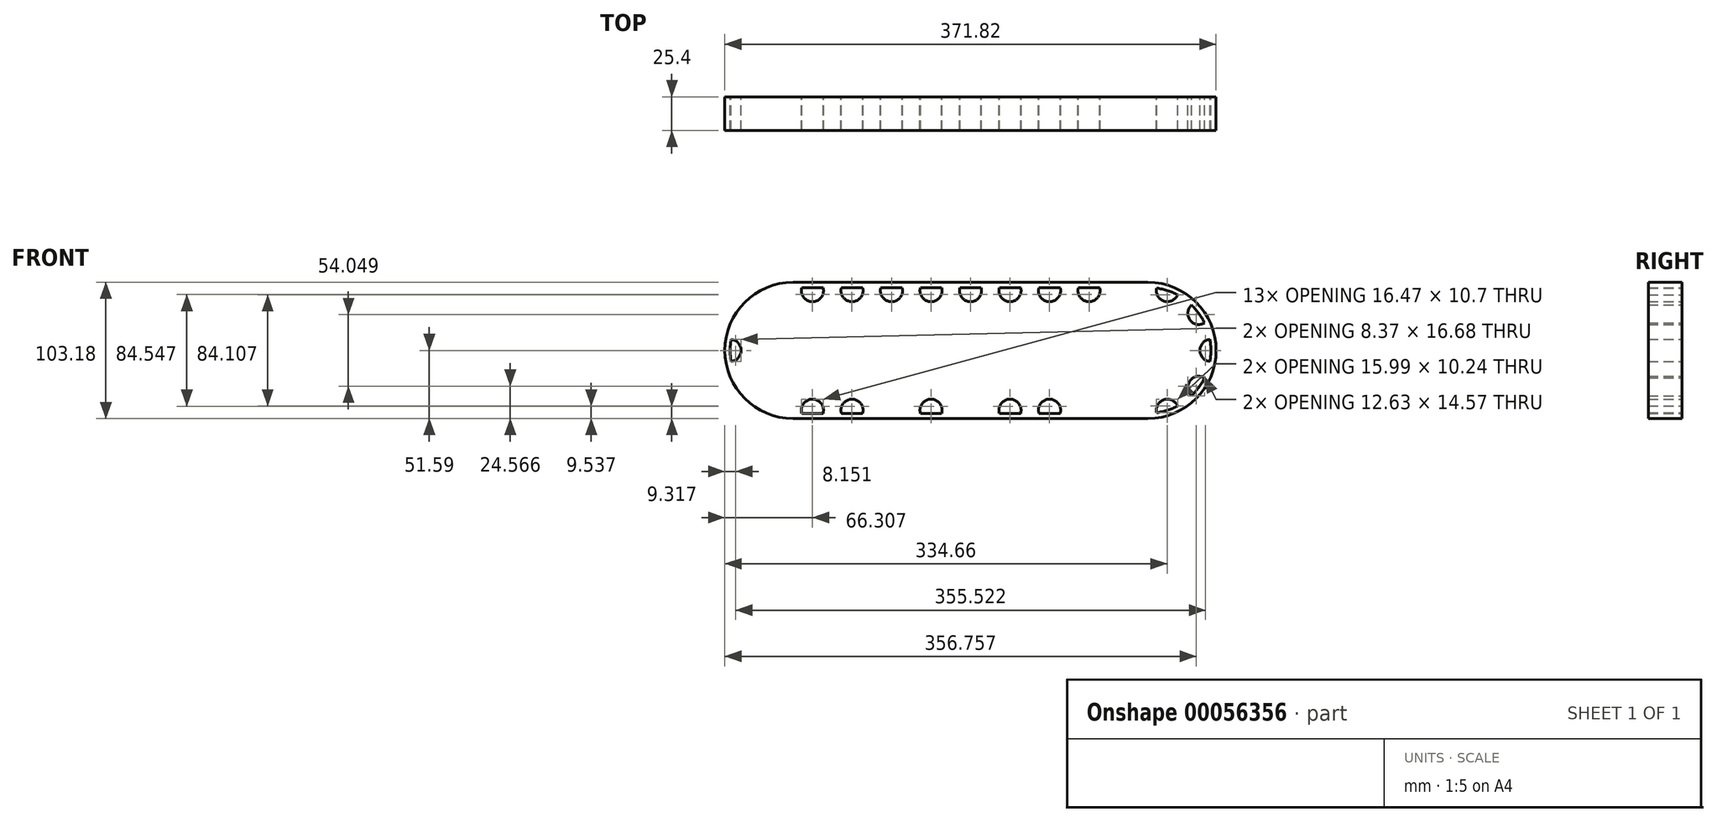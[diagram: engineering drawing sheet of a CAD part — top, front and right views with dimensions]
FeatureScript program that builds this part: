
annotation { "Feature Type Name" : "Feature", "Feature Type Description" : "" }
export const myFeature = defineFeature(function(context is Context, id is Id, definition is map)
    precondition{}
    {
        {
            var Q0;
            Q0=qCreatedBy(makeId("Front.planeOp"),FACE);
            var sketch = newSketch(context, id + "F0", { "sketchPlane" : qUnion([Q0])});
            skCircle(sketch, "E0", {"center": v(0, 0) * mm, "radius": 9.53 * mm});
            skCircle(sketch, "E1", {"center": v(0, 0) * mm, "radius": 15.88 * mm});
            skCircle(sketch, "E2", {"center": v(0, 0) * mm, "radius": 25.4 * mm});
            skCircle(sketch, "E3", {"center": v(0, 0) * mm, "radius": 38.1 * mm});
            skArc(sketch, "E4", {"start": v(5.87, 47.26) * mm, "mid": v(0, 47.63) * mm, "end": v(-5.87, 47.26) * mm});
            skLineSegment(sketch, "E5", {"start": v(-5.87, 47.26) * mm, "end": v(-7.62, 37.33) * mm});
            skLineSegment(sketch, "E6", {"start": v(5.87, 47.26) * mm, "end": v(7.62, 37.33) * mm});
            skLineSegment(sketch, "E7", {"start": v(-3.98, 25.09) * mm, "end": v(-3.98, 15.37) * mm, "construction": true});
            skLineSegment(sketch, "E8", {"start": v(3.98, 25.09) * mm, "end": v(3.98, 15.37) * mm, "construction": true});
            skArc(sketch, "E9.1.0", {"start": v(-23.03, 41.69) * mm, "mid": v(-28, 38.53) * mm, "end": v(-32.53, 34.79) * mm});
            skLineSegment(sketch, "E9.1.1", {"start": v(-32.53, 34.79) * mm, "end": v(-28.1, 25.72) * mm});
            skLineSegment(sketch, "E9.1.2", {"start": v(-23.03, 41.69) * mm, "end": v(-15.78, 34.68) * mm});
            skArc(sketch, "E9.2.0", {"start": v(-43.14, 20.19) * mm, "mid": v(-45.3, 14.72) * mm, "end": v(-46.76, 9.02) * mm});
            skLineSegment(sketch, "E9.2.1", {"start": v(-46.76, 9.02) * mm, "end": v(-37.86, 4.29) * mm});
            skLineSegment(sketch, "E9.2.2", {"start": v(-43.14, 20.19) * mm, "end": v(-33.15, 18.78) * mm});
            skArc(sketch, "E9.3.0", {"start": v(-46.76, -9.02) * mm, "mid": v(-45.3, -14.72) * mm, "end": v(-43.14, -20.19) * mm});
            skLineSegment(sketch, "E9.3.1", {"start": v(-43.14, -20.19) * mm, "end": v(-33.15, -18.78) * mm});
            skLineSegment(sketch, "E9.3.2", {"start": v(-46.76, -9.02) * mm, "end": v(-37.86, -4.29) * mm});
            skArc(sketch, "E9.4.0", {"start": v(-32.53, -34.79) * mm, "mid": v(-28, -38.53) * mm, "end": v(-23.03, -41.69) * mm});
            skLineSegment(sketch, "E9.4.1", {"start": v(-23.03, -41.69) * mm, "end": v(-15.78, -34.68) * mm});
            skLineSegment(sketch, "E9.4.2", {"start": v(-32.53, -34.79) * mm, "end": v(-28.1, -25.72) * mm});
            skArc(sketch, "E9.5.0", {"start": v(-5.87, -47.26) * mm, "mid": v(0, -47.63) * mm, "end": v(5.87, -47.26) * mm});
            skLineSegment(sketch, "E9.5.1", {"start": v(5.87, -47.26) * mm, "end": v(7.62, -37.33) * mm});
            skLineSegment(sketch, "E9.5.2", {"start": v(-5.87, -47.26) * mm, "end": v(-7.62, -37.33) * mm});
            skArc(sketch, "E9.6.0", {"start": v(23.03, -41.69) * mm, "mid": v(28, -38.53) * mm, "end": v(32.53, -34.79) * mm});
            skLineSegment(sketch, "E9.6.1", {"start": v(32.53, -34.79) * mm, "end": v(28.1, -25.72) * mm});
            skLineSegment(sketch, "E9.6.2", {"start": v(23.03, -41.69) * mm, "end": v(15.78, -34.68) * mm});
            skArc(sketch, "E9.7.0", {"start": v(43.14, -20.19) * mm, "mid": v(45.3, -14.72) * mm, "end": v(46.76, -9.02) * mm});
            skLineSegment(sketch, "E9.7.1", {"start": v(46.76, -9.02) * mm, "end": v(37.86, -4.29) * mm});
            skLineSegment(sketch, "E9.7.2", {"start": v(43.14, -20.19) * mm, "end": v(33.15, -18.78) * mm});
            skArc(sketch, "E9.8.0", {"start": v(46.76, 9.02) * mm, "mid": v(45.3, 14.72) * mm, "end": v(43.14, 20.19) * mm});
            skLineSegment(sketch, "E9.8.1", {"start": v(43.14, 20.19) * mm, "end": v(33.15, 18.78) * mm});
            skLineSegment(sketch, "E9.8.2", {"start": v(46.76, 9.02) * mm, "end": v(37.86, 4.29) * mm});
            skArc(sketch, "E9.9.0", {"start": v(32.53, 34.79) * mm, "mid": v(28, 38.53) * mm, "end": v(23.03, 41.69) * mm});
            skLineSegment(sketch, "E9.9.1", {"start": v(23.03, 41.69) * mm, "end": v(15.78, 34.68) * mm});
            skLineSegment(sketch, "E9.9.2", {"start": v(32.53, 34.79) * mm, "end": v(28.1, 25.72) * mm});
            skLineSegment(sketch, "E10.1.0", {"start": v(-19.74, -15.99) * mm, "end": v(-11.32, -11.13) * mm, "construction": true});
            skLineSegment(sketch, "E10.1.1", {"start": v(-23.71, -9.1) * mm, "end": v(-15.3, -4.24) * mm, "construction": true});
            skLineSegment(sketch, "E10.2.0", {"start": v(23.71, -9.1) * mm, "end": v(15.3, -4.24) * mm, "construction": true});
            skLineSegment(sketch, "E10.2.1", {"start": v(19.74, -15.99) * mm, "end": v(11.32, -11.13) * mm, "construction": true});
            skSolve(sketch);
        }
        {
            var Q0;
            Q0=qCreatedBy(makeId("Front.planeOp"),FACE);
            var sketch = newSketch(context, id + "F1", { "sketchPlane" : qUnion([Q0])});
            skArc(sketch, "E11", {"start": v(23.03, 41.69) * mm, "mid": v(-10.34, 46.49) * mm, "end": v(-38.53, 28) * mm});
            skLineSegment(sketch, "E12.0", {"start": v(23.03, 41.69) * mm, "end": v(15.78, 34.68) * mm, "construction": true});
            skLineSegment(sketch, "E12.1", {"start": v(5.87, 47.26) * mm, "end": v(7.62, 37.33) * mm, "construction": true});
            skLineSegment(sketch, "E12.2", {"start": v(-5.87, 47.26) * mm, "end": v(-7.62, 37.33) * mm, "construction": true});
            skLineSegment(sketch, "E12.3", {"start": v(-23.03, 41.69) * mm, "end": v(-15.78, 34.68) * mm, "construction": true});
            skLineSegment(sketch, "E12.4", {"start": v(-32.53, 34.79) * mm, "end": v(-28.1, 25.72) * mm, "construction": true});
            skLineSegment(sketch, "E12.5", {"start": v(-43.14, 20.19) * mm, "end": v(-33.15, 18.78) * mm, "construction": true});
            skLineSegment(sketch, "E12.6", {"start": v(-46.76, 9.02) * mm, "end": v(-37.86, 4.29) * mm, "construction": true});
            skLineSegment(sketch, "E12.7", {"start": v(-46.76, -9.02) * mm, "end": v(-37.86, -4.29) * mm, "construction": true});
            skCircle(sketch, "E13", {"center": v(-14.72, 45.3) * mm, "radius": 8.37 * mm});
            skCircle(sketch, "E14", {"center": v(-38.53, 28) * mm, "radius": 8.37 * mm});
            skCircle(sketch, "E15", {"center": v(-47.63, 0) * mm, "radius": 8.37 * mm});
            skCircle(sketch, "E16", {"center": v(14.72, 45.3) * mm, "radius": 8.37 * mm});
            skLineSegment(sketch, "E17", {"start": v(-14.72, 45.3) * mm, "end": v(14.72, 45.3) * mm, "construction": true});
            skArc(sketch, "E18.trimOffspring", {"start": v(-42.84, 20.81) * mm, "mid": v(-45.3, 14.72) * mm, "end": v(-46.89, 8.34) * mm});
            skArc(sketch, "E19.trimOffspring", {"start": v(-47.63, 0) * mm, "mid": v(-24.2, -41.02) * mm, "end": v(23.03, -41.69) * mm});
            skLineSegment(sketch, "E20", {"start": v(14.72, 45.3) * mm, "end": v(44.62, 45.3) * mm, "construction": true});
            skLineSegment(sketch, "E21", {"start": v(44.62, 45.3) * mm, "end": v(74.52, 45.3) * mm, "construction": true});
            skLineSegment(sketch, "E22", {"start": v(74.52, 45.3) * mm, "end": v(104.42, 45.3) * mm, "construction": true});
            skLineSegment(sketch, "E23", {"start": v(104.42, 45.3) * mm, "end": v(134.32, 45.3) * mm, "construction": true});
            skCircle(sketch, "E24", {"center": v(44.62, 45.3) * mm, "radius": 8.37 * mm});
            skCircle(sketch, "E25", {"center": v(74.52, 45.3) * mm, "radius": 8.37 * mm});
            skCircle(sketch, "E26", {"center": v(104.42, 45.3) * mm, "radius": 8.37 * mm});
            skCircle(sketch, "E27", {"center": v(134.32, 45.3) * mm, "radius": 8.37 * mm});
            skPoint(sketch, "E28", {"position": v(23.09, 45.3) * mm});
            skPoint(sketch, "E29", {"position": v(36.25, 45.3) * mm});
            skLineSegment(sketch, "E30", {"start": v(0, 0) * mm, "end": v(134.32, 0) * mm, "construction": true});
            skLineSegment(sketch, "E31", {"start": v(134.32, 45.3) * mm, "end": v(134.32, 0) * mm, "construction": true});
            skCircle(sketch, "E32.MirrorC", {"center": v(134.32, -45.3) * mm, "radius": 8.37 * mm});
            skCircle(sketch, "E33.MirrorC", {"center": v(104.42, -45.3) * mm, "radius": 8.37 * mm});
            skCircle(sketch, "E34.MirrorC", {"center": v(74.52, -45.3) * mm, "radius": 8.37 * mm});
            skCircle(sketch, "E35.MirrorC", {"center": v(44.62, -45.3) * mm, "radius": 8.37 * mm});
            skCircle(sketch, "E36.MirrorC", {"center": v(14.72, -45.3) * mm, "radius": 8.37 * mm});
            skCircle(sketch, "E37.MirrorC", {"center": v(-14.72, -45.3) * mm, "radius": 8.37 * mm});
            skCircle(sketch, "E38.MirrorC", {"center": v(-38.53, -28) * mm, "radius": 8.37 * mm});
            skCircle(sketch, "E39.MirrorC", {"center": v(164.22, 45.3) * mm, "radius": 8.37 * mm});
            skCircle(sketch, "E40.MirrorC", {"center": v(194.12, 45.3) * mm, "radius": 8.37 * mm});
            skCircle(sketch, "E41.MirrorC", {"center": v(224.03, 45.3) * mm, "radius": 8.37 * mm});
            skCircle(sketch, "E42.MirrorC", {"center": v(253.93, 45.3) * mm, "radius": 8.37 * mm});
            skCircle(sketch, "E43.MirrorC", {"center": v(283.36, 45.3) * mm, "radius": 8.37 * mm});
            skCircle(sketch, "E44.MirrorC", {"center": v(307.17, 28) * mm, "radius": 8.37 * mm});
            skCircle(sketch, "E45.MirrorC", {"center": v(316.27, 0) * mm, "radius": 8.37 * mm});
            skCircle(sketch, "E46.MirrorC", {"center": v(307.17, -28) * mm, "radius": 8.37 * mm});
            skCircle(sketch, "E47.MirrorC", {"center": v(283.36, -45.3) * mm, "radius": 8.37 * mm});
            skCircle(sketch, "E48.MirrorC", {"center": v(253.93, -45.3) * mm, "radius": 8.37 * mm});
            skCircle(sketch, "E49.MirrorC", {"center": v(224.03, -45.3) * mm, "radius": 8.37 * mm});
            skCircle(sketch, "E50.MirrorC", {"center": v(194.12, -45.3) * mm, "radius": 8.37 * mm});
            skCircle(sketch, "E51.MirrorC", {"center": v(164.22, -45.3) * mm, "radius": 8.37 * mm});
            skSolve(sketch);
        }
        {
            var Q0;
            Q0=qCreatedBy(makeId("Front.planeOp"),FACE);
            var sketch = newSketch(context, id + "F2", { "sketchPlane" : qUnion([Q0])});
            skArc(sketch, "E52", {"start": v(0, 47.63) * mm, "mid": v(-47.63, 0) * mm, "end": v(0, -47.63) * mm});
            skLineSegment(sketch, "E53", {"start": v(0, 47.63) * mm, "end": v(268.64, 47.63) * mm});
            skLineSegment(sketch, "E54", {"start": v(0, -47.63) * mm, "end": v(268.64, -47.63) * mm});
            skLineSegment(sketch, "E55.0", {"start": v(0, 0) * mm, "end": v(134.32, 0) * mm, "construction": true});
            skLineSegment(sketch, "E56.0", {"start": v(134.32, 45.3) * mm, "end": v(134.32, 0) * mm, "construction": true});
            skLineSegment(sketch, "E57.MirrorCS", {"start": v(268.64, 0) * mm, "end": v(134.32, 0) * mm, "construction": true});
            skArc(sketch, "E58", {"start": v(268.64, 47.63) * mm, "mid": v(316.27, 0) * mm, "end": v(268.64, -47.63) * mm});
            skLineSegment(sketch, "E59.0", {"start": v(0, 51.59) * mm, "end": v(268.64, 51.59) * mm});
            skArc(sketch, "E59.1", {"start": v(0, 51.59) * mm, "mid": v(-51.59, 0) * mm, "end": v(0, -51.59) * mm});
            skLineSegment(sketch, "E59.2", {"start": v(0, -51.59) * mm, "end": v(268.64, -51.59) * mm});
            skArc(sketch, "E59.3", {"start": v(268.64, 51.59) * mm, "mid": v(320.23, 0) * mm, "end": v(268.64, -51.59) * mm});
            skArc(sketch, "E60.0", {"start": v(-23.04, 46.15) * mm, "mid": v(-12.13, 37.33) * mm, "end": v(-8.49, 50.88) * mm});
            skArc(sketch, "E60.1", {"start": v(9.2, 51.59) * mm, "mid": v(14.72, 36.92) * mm, "end": v(20.24, 51.59) * mm});
            skArc(sketch, "E60.2", {"start": v(39.1, 51.59) * mm, "mid": v(44.62, 36.92) * mm, "end": v(50.14, 51.59) * mm});
            skArc(sketch, "E60.3", {"start": v(69, 51.59) * mm, "mid": v(74.52, 36.92) * mm, "end": v(80.04, 51.59) * mm});
            skArc(sketch, "E60.4", {"start": v(98.9, 51.59) * mm, "mid": v(104.42, 36.92) * mm, "end": v(109.94, 51.59) * mm});
            skArc(sketch, "E60.5", {"start": v(128.8, 51.59) * mm, "mid": v(134.32, 36.92) * mm, "end": v(139.84, 51.59) * mm});
            skArc(sketch, "E60.6", {"start": v(169.74, 51.59) * mm, "mid": v(164.22, 36.92) * mm, "end": v(158.7, 51.59) * mm});
            skArc(sketch, "E60.7", {"start": v(199.65, 51.59) * mm, "mid": v(194.12, 36.92) * mm, "end": v(188.6, 51.59) * mm});
            skArc(sketch, "E60.8", {"start": v(229.55, 51.59) * mm, "mid": v(224.03, 36.92) * mm, "end": v(218.5, 51.59) * mm});
            skArc(sketch, "E60.9", {"start": v(259.45, 51.59) * mm, "mid": v(253.93, 36.92) * mm, "end": v(248.4, 51.59) * mm});
            skArc(sketch, "E60.10", {"start": v(291.69, 46.15) * mm, "mid": v(280.77, 37.33) * mm, "end": v(277.13, 50.88) * mm});
            skArc(sketch, "E60.11", {"start": v(314.42, 23.8) * mm, "mid": v(300.4, 23.07) * mm, "end": v(305.42, 36.18) * mm});
            skArc(sketch, "E60.12", {"start": v(319.66, -7.65) * mm, "mid": v(307.9, 0) * mm, "end": v(319.66, 7.65) * mm});
            skArc(sketch, "E60.13", {"start": v(314.42, -23.8) * mm, "mid": v(300.4, -23.07) * mm, "end": v(305.42, -36.18) * mm});
            skArc(sketch, "E60.14", {"start": v(291.69, -46.15) * mm, "mid": v(280.77, -37.33) * mm, "end": v(277.13, -50.88) * mm});
            skArc(sketch, "E60.15", {"start": v(259.45, -51.59) * mm, "mid": v(253.93, -36.92) * mm, "end": v(248.4, -51.59) * mm});
            skArc(sketch, "E60.16", {"start": v(229.55, -51.59) * mm, "mid": v(224.03, -36.92) * mm, "end": v(218.5, -51.59) * mm});
            skArc(sketch, "E60.17", {"start": v(199.65, -51.59) * mm, "mid": v(194.12, -36.92) * mm, "end": v(188.6, -51.59) * mm});
            skArc(sketch, "E60.18", {"start": v(169.74, -51.59) * mm, "mid": v(164.22, -36.92) * mm, "end": v(158.7, -51.59) * mm});
            skArc(sketch, "E60.19", {"start": v(128.8, -51.59) * mm, "mid": v(134.32, -36.92) * mm, "end": v(139.84, -51.59) * mm});
            skArc(sketch, "E60.20", {"start": v(98.9, -51.59) * mm, "mid": v(104.42, -36.92) * mm, "end": v(109.94, -51.59) * mm});
            skArc(sketch, "E60.21", {"start": v(69, -51.59) * mm, "mid": v(74.52, -36.92) * mm, "end": v(80.04, -51.59) * mm});
            skArc(sketch, "E60.22", {"start": v(39.1, -51.59) * mm, "mid": v(44.62, -36.92) * mm, "end": v(50.14, -51.59) * mm});
            skArc(sketch, "E60.23", {"start": v(9.2, -51.59) * mm, "mid": v(14.72, -36.92) * mm, "end": v(20.24, -51.59) * mm});
            skArc(sketch, "E60.24", {"start": v(-23.04, -46.15) * mm, "mid": v(-12.13, -37.33) * mm, "end": v(-8.49, -50.88) * mm});
            skArc(sketch, "E60.25", {"start": v(-45.77, -23.8) * mm, "mid": v(-31.76, -23.07) * mm, "end": v(-36.77, -36.18) * mm});
            skArc(sketch, "E60.26", {"start": v(-51.02, -7.65) * mm, "mid": v(-39.25, 0) * mm, "end": v(-51.02, 7.65) * mm});
            skArc(sketch, "E60.27", {"start": v(-45.77, 23.8) * mm, "mid": v(-31.76, 23.07) * mm, "end": v(-36.77, 36.18) * mm});
            skSolve(sketch);
        }
        {
            var Q0;
            Q0 = qSketchRegion(id + "F2", true);
            var Q1;
            {var subQ0=sQuery(id+"F2.wireOp",EDGE,"E60.26");var subQ1=sQuery(id+"F2.wireOp",EDGE,"E52");var subQ2=makeQuery(id+"F2.imprint","INTERSECT",VERTEX,{"disambiguationData":[OD(0.0)],"derivedFrom":[subQ1,subQ0]});Q1=makeQuery(id+"F2.imprint","IMPRINT",FACE,{"disambiguationData":[TD([[makeQuery(id+"F2.imprint","IMPRINT",EDGE,{"disambiguationData":[TD([[subQ2,-1.0]])],"derivedFrom":subQ1}),1.0]])]});}
            var Q2;
            {var subQ0=sQuery(id+"F2.wireOp",EDGE,"E60.25");var subQ1=sQuery(id+"F2.wireOp",EDGE,"E52");var subQ2=makeQuery(id+"F2.imprint","INTERSECT",VERTEX,{"disambiguationData":[OD(0.0)],"derivedFrom":[subQ1,subQ0]});Q2=makeQuery(id+"F2.imprint","IMPRINT",FACE,{"disambiguationData":[TD([[makeQuery(id+"F2.imprint","IMPRINT",EDGE,{"disambiguationData":[TD([[subQ2,-1.0]])],"derivedFrom":subQ1}),1.0]])]});}
            var Q3;
            {var subQ0=sQuery(id+"F2.wireOp",EDGE,"E60.24");var subQ1=sQuery(id+"F2.wireOp",EDGE,"E52");var subQ2=makeQuery(id+"F2.imprint","INTERSECT",VERTEX,{"disambiguationData":[OD(0.0)],"derivedFrom":[subQ1,subQ0]});Q3=makeQuery(id+"F2.imprint","IMPRINT",FACE,{"disambiguationData":[TD([[makeQuery(id+"F2.imprint","IMPRINT",EDGE,{"disambiguationData":[TD([[subQ2,-1.0]])],"derivedFrom":subQ1}),1.0]])]});}
            var Q4;
            {var subQ0=sQuery(id+"F2.wireOp",EDGE,"E60.23");var subQ1=sQuery(id+"F2.wireOp",EDGE,"E54");var subQ2=makeQuery(id+"F2.imprint","INTERSECT",VERTEX,{"disambiguationData":[OD(0.0)],"derivedFrom":[subQ1,subQ0]});Q4=makeQuery(id+"F2.imprint","IMPRINT",FACE,{"disambiguationData":[TD([[makeQuery(id+"F2.imprint","IMPRINT",EDGE,{"disambiguationData":[TD([[subQ2,-1.0]])],"derivedFrom":subQ1}),1.0]])]});}
            var Q5;
            {var subQ0=sQuery(id+"F2.wireOp",EDGE,"E60.22");var subQ1=sQuery(id+"F2.wireOp",EDGE,"E54");var subQ2=makeQuery(id+"F2.imprint","INTERSECT",VERTEX,{"disambiguationData":[OD(0.0)],"derivedFrom":[subQ1,subQ0]});Q5=makeQuery(id+"F2.imprint","IMPRINT",FACE,{"disambiguationData":[TD([[makeQuery(id+"F2.imprint","IMPRINT",EDGE,{"disambiguationData":[TD([[subQ2,-1.0]])],"derivedFrom":subQ1}),1.0]])]});}
            var Q6;
            {var subQ0=sQuery(id+"F2.wireOp",EDGE,"E60.21");var subQ1=sQuery(id+"F2.wireOp",EDGE,"E54");var subQ2=makeQuery(id+"F2.imprint","INTERSECT",VERTEX,{"disambiguationData":[OD(0.0)],"derivedFrom":[subQ1,subQ0]});Q6=makeQuery(id+"F2.imprint","IMPRINT",FACE,{"disambiguationData":[TD([[makeQuery(id+"F2.imprint","IMPRINT",EDGE,{"disambiguationData":[TD([[subQ2,-1.0]])],"derivedFrom":subQ1}),1.0]])]});}
            var Q7;
            {var subQ0=sQuery(id+"F2.wireOp",EDGE,"E60.20");var subQ1=sQuery(id+"F2.wireOp",EDGE,"E54");var subQ2=makeQuery(id+"F2.imprint","INTERSECT",VERTEX,{"disambiguationData":[OD(0.0)],"derivedFrom":[subQ1,subQ0]});Q7=makeQuery(id+"F2.imprint","IMPRINT",FACE,{"disambiguationData":[TD([[makeQuery(id+"F2.imprint","IMPRINT",EDGE,{"disambiguationData":[TD([[subQ2,-1.0]])],"derivedFrom":subQ1}),1.0]])]});}
            var Q8;
            {var subQ0=sQuery(id+"F2.wireOp",EDGE,"E60.19");var subQ1=sQuery(id+"F2.wireOp",EDGE,"E54");var subQ2=makeQuery(id+"F2.imprint","INTERSECT",VERTEX,{"disambiguationData":[OD(0.0)],"derivedFrom":[subQ1,subQ0]});Q8=makeQuery(id+"F2.imprint","IMPRINT",FACE,{"disambiguationData":[TD([[makeQuery(id+"F2.imprint","IMPRINT",EDGE,{"disambiguationData":[TD([[subQ2,-1.0]])],"derivedFrom":subQ1}),1.0]])]});}
            var Q9;
            {var subQ0=sQuery(id+"F2.wireOp",EDGE,"E60.18");var subQ1=sQuery(id+"F2.wireOp",EDGE,"E54");var subQ2=makeQuery(id+"F2.imprint","INTERSECT",VERTEX,{"disambiguationData":[OD(0.0)],"derivedFrom":[subQ1,subQ0]});Q9=makeQuery(id+"F2.imprint","IMPRINT",FACE,{"disambiguationData":[TD([[makeQuery(id+"F2.imprint","IMPRINT",EDGE,{"disambiguationData":[TD([[subQ2,-1.0]])],"derivedFrom":subQ1}),1.0]])]});}
            var Q10;
            {var subQ0=sQuery(id+"F2.wireOp",EDGE,"E60.17");var subQ1=sQuery(id+"F2.wireOp",EDGE,"E54");var subQ2=makeQuery(id+"F2.imprint","INTERSECT",VERTEX,{"disambiguationData":[OD(0.0)],"derivedFrom":[subQ1,subQ0]});Q10=makeQuery(id+"F2.imprint","IMPRINT",FACE,{"disambiguationData":[TD([[makeQuery(id+"F2.imprint","IMPRINT",EDGE,{"disambiguationData":[TD([[subQ2,-1.0]])],"derivedFrom":subQ1}),1.0]])]});}
            var Q11;
            {var subQ0=sQuery(id+"F2.wireOp",EDGE,"E60.16");var subQ1=sQuery(id+"F2.wireOp",EDGE,"E54");var subQ2=makeQuery(id+"F2.imprint","INTERSECT",VERTEX,{"disambiguationData":[OD(0.0)],"derivedFrom":[subQ1,subQ0]});Q11=makeQuery(id+"F2.imprint","IMPRINT",FACE,{"disambiguationData":[TD([[makeQuery(id+"F2.imprint","IMPRINT",EDGE,{"disambiguationData":[TD([[subQ2,-1.0]])],"derivedFrom":subQ1}),1.0]])]});}
            var Q12;
            {var subQ0=sQuery(id+"F2.wireOp",EDGE,"E60.15");var subQ1=sQuery(id+"F2.wireOp",EDGE,"E54");var subQ2=makeQuery(id+"F2.imprint","INTERSECT",VERTEX,{"disambiguationData":[OD(0.0)],"derivedFrom":[subQ1,subQ0]});Q12=makeQuery(id+"F2.imprint","IMPRINT",FACE,{"disambiguationData":[TD([[makeQuery(id+"F2.imprint","IMPRINT",EDGE,{"disambiguationData":[TD([[subQ2,-1.0]])],"derivedFrom":subQ1}),1.0]])]});}
            var Q13;
            {var subQ0=sQuery(id+"F2.wireOp",EDGE,"E60.14");var subQ1=sQuery(id+"F2.wireOp",EDGE,"E58");var subQ2=makeQuery(id+"F2.imprint","INTERSECT",VERTEX,{"disambiguationData":[OD(0.0)],"derivedFrom":[subQ1,subQ0]});Q13=makeQuery(id+"F2.imprint","IMPRINT",FACE,{"disambiguationData":[TD([[makeQuery(id+"F2.imprint","IMPRINT",EDGE,{"disambiguationData":[TD([[subQ2,-1.0]])],"derivedFrom":subQ1}),-1.0]])]});}
            var Q14;
            {var subQ0=sQuery(id+"F2.wireOp",EDGE,"E60.13");var subQ1=sQuery(id+"F2.wireOp",EDGE,"E58");var subQ2=makeQuery(id+"F2.imprint","INTERSECT",VERTEX,{"disambiguationData":[OD(0.0)],"derivedFrom":[subQ1,subQ0]});Q14=makeQuery(id+"F2.imprint","IMPRINT",FACE,{"disambiguationData":[TD([[makeQuery(id+"F2.imprint","IMPRINT",EDGE,{"disambiguationData":[TD([[subQ2,-1.0]])],"derivedFrom":subQ1}),-1.0]])]});}
            var Q15;
            {var subQ0=sQuery(id+"F2.wireOp",EDGE,"E60.12");var subQ1=sQuery(id+"F2.wireOp",EDGE,"E58");var subQ2=makeQuery(id+"F2.imprint","INTERSECT",VERTEX,{"disambiguationData":[OD(0.0)],"derivedFrom":[subQ1,subQ0]});Q15=makeQuery(id+"F2.imprint","IMPRINT",FACE,{"disambiguationData":[TD([[makeQuery(id+"F2.imprint","IMPRINT",EDGE,{"disambiguationData":[TD([[subQ2,-1.0]])],"derivedFrom":subQ1}),-1.0]])]});}
            var Q16;
            {var subQ0=sQuery(id+"F2.wireOp",EDGE,"E60.11");var subQ1=sQuery(id+"F2.wireOp",EDGE,"E58");var subQ2=makeQuery(id+"F2.imprint","INTERSECT",VERTEX,{"disambiguationData":[OD(0.0)],"derivedFrom":[subQ1,subQ0]});Q16=makeQuery(id+"F2.imprint","IMPRINT",FACE,{"disambiguationData":[TD([[makeQuery(id+"F2.imprint","IMPRINT",EDGE,{"disambiguationData":[TD([[subQ2,-1.0]])],"derivedFrom":subQ1}),-1.0]])]});}
            var Q17;
            {var subQ0=sQuery(id+"F2.wireOp",EDGE,"E60.10");var subQ1=sQuery(id+"F2.wireOp",EDGE,"E58");var subQ2=makeQuery(id+"F2.imprint","INTERSECT",VERTEX,{"disambiguationData":[OD(0.0)],"derivedFrom":[subQ1,subQ0]});Q17=makeQuery(id+"F2.imprint","IMPRINT",FACE,{"disambiguationData":[TD([[makeQuery(id+"F2.imprint","IMPRINT",EDGE,{"disambiguationData":[TD([[subQ2,-1.0]])],"derivedFrom":subQ1}),-1.0]])]});}
            var Q18;
            {var subQ0=sQuery(id+"F2.wireOp",EDGE,"E60.9");var subQ1=sQuery(id+"F2.wireOp",EDGE,"E53");var subQ2=makeQuery(id+"F2.imprint","INTERSECT",VERTEX,{"disambiguationData":[OD(0.0)],"derivedFrom":[subQ1,subQ0]});Q18=makeQuery(id+"F2.imprint","IMPRINT",FACE,{"disambiguationData":[TD([[makeQuery(id+"F2.imprint","IMPRINT",EDGE,{"disambiguationData":[TD([[subQ2,-1.0]])],"derivedFrom":subQ1}),-1.0]])]});}
            var Q19;
            {var subQ0=sQuery(id+"F2.wireOp",EDGE,"E60.8");var subQ1=sQuery(id+"F2.wireOp",EDGE,"E53");var subQ2=makeQuery(id+"F2.imprint","INTERSECT",VERTEX,{"disambiguationData":[OD(0.0)],"derivedFrom":[subQ1,subQ0]});Q19=makeQuery(id+"F2.imprint","IMPRINT",FACE,{"disambiguationData":[TD([[makeQuery(id+"F2.imprint","IMPRINT",EDGE,{"disambiguationData":[TD([[subQ2,-1.0]])],"derivedFrom":subQ1}),-1.0]])]});}
            var Q20;
            {var subQ0=sQuery(id+"F2.wireOp",EDGE,"E60.7");var subQ1=sQuery(id+"F2.wireOp",EDGE,"E53");var subQ2=makeQuery(id+"F2.imprint","INTERSECT",VERTEX,{"disambiguationData":[OD(0.0)],"derivedFrom":[subQ1,subQ0]});Q20=makeQuery(id+"F2.imprint","IMPRINT",FACE,{"disambiguationData":[TD([[makeQuery(id+"F2.imprint","IMPRINT",EDGE,{"disambiguationData":[TD([[subQ2,-1.0]])],"derivedFrom":subQ1}),-1.0]])]});}
            var Q21;
            {var subQ0=sQuery(id+"F2.wireOp",EDGE,"E60.6");var subQ1=sQuery(id+"F2.wireOp",EDGE,"E53");var subQ2=makeQuery(id+"F2.imprint","INTERSECT",VERTEX,{"disambiguationData":[OD(0.0)],"derivedFrom":[subQ1,subQ0]});Q21=makeQuery(id+"F2.imprint","IMPRINT",FACE,{"disambiguationData":[TD([[makeQuery(id+"F2.imprint","IMPRINT",EDGE,{"disambiguationData":[TD([[subQ2,-1.0]])],"derivedFrom":subQ1}),-1.0]])]});}
            var Q22;
            {var subQ0=sQuery(id+"F2.wireOp",EDGE,"E60.5");var subQ1=sQuery(id+"F2.wireOp",EDGE,"E53");var subQ2=makeQuery(id+"F2.imprint","INTERSECT",VERTEX,{"disambiguationData":[OD(0.0)],"derivedFrom":[subQ1,subQ0]});Q22=makeQuery(id+"F2.imprint","IMPRINT",FACE,{"disambiguationData":[TD([[makeQuery(id+"F2.imprint","IMPRINT",EDGE,{"disambiguationData":[TD([[subQ2,-1.0]])],"derivedFrom":subQ1}),-1.0]])]});}
            var Q23;
            {var subQ0=sQuery(id+"F2.wireOp",EDGE,"E60.4");var subQ1=sQuery(id+"F2.wireOp",EDGE,"E53");var subQ2=makeQuery(id+"F2.imprint","INTERSECT",VERTEX,{"disambiguationData":[OD(0.0)],"derivedFrom":[subQ1,subQ0]});Q23=makeQuery(id+"F2.imprint","IMPRINT",FACE,{"disambiguationData":[TD([[makeQuery(id+"F2.imprint","IMPRINT",EDGE,{"disambiguationData":[TD([[subQ2,-1.0]])],"derivedFrom":subQ1}),-1.0]])]});}
            var Q24;
            {var subQ0=sQuery(id+"F2.wireOp",EDGE,"E60.3");var subQ1=sQuery(id+"F2.wireOp",EDGE,"E53");var subQ2=makeQuery(id+"F2.imprint","INTERSECT",VERTEX,{"disambiguationData":[OD(0.0)],"derivedFrom":[subQ1,subQ0]});Q24=makeQuery(id+"F2.imprint","IMPRINT",FACE,{"disambiguationData":[TD([[makeQuery(id+"F2.imprint","IMPRINT",EDGE,{"disambiguationData":[TD([[subQ2,-1.0]])],"derivedFrom":subQ1}),-1.0]])]});}
            var Q25;
            {var subQ0=sQuery(id+"F2.wireOp",EDGE,"E60.2");var subQ1=sQuery(id+"F2.wireOp",EDGE,"E53");var subQ2=makeQuery(id+"F2.imprint","INTERSECT",VERTEX,{"disambiguationData":[OD(0.0)],"derivedFrom":[subQ1,subQ0]});Q25=makeQuery(id+"F2.imprint","IMPRINT",FACE,{"disambiguationData":[TD([[makeQuery(id+"F2.imprint","IMPRINT",EDGE,{"disambiguationData":[TD([[subQ2,-1.0]])],"derivedFrom":subQ1}),-1.0]])]});}
            var Q26;
            {var subQ0=sQuery(id+"F2.wireOp",EDGE,"E60.1");var subQ1=sQuery(id+"F2.wireOp",EDGE,"E53");var subQ2=makeQuery(id+"F2.imprint","INTERSECT",VERTEX,{"disambiguationData":[OD(0.0)],"derivedFrom":[subQ1,subQ0]});Q26=makeQuery(id+"F2.imprint","IMPRINT",FACE,{"disambiguationData":[TD([[makeQuery(id+"F2.imprint","IMPRINT",EDGE,{"disambiguationData":[TD([[subQ2,-1.0]])],"derivedFrom":subQ1}),-1.0]])]});}
            var Q27;
            {var subQ0=sQuery(id+"F2.wireOp",EDGE,"E60.0");var subQ1=sQuery(id+"F2.wireOp",EDGE,"E52");var subQ2=makeQuery(id+"F2.imprint","INTERSECT",VERTEX,{"disambiguationData":[OD(0.0)],"derivedFrom":[subQ1,subQ0]});Q27=makeQuery(id+"F2.imprint","IMPRINT",FACE,{"disambiguationData":[TD([[makeQuery(id+"F2.imprint","IMPRINT",EDGE,{"disambiguationData":[TD([[subQ2,-1.0]])],"derivedFrom":subQ1}),1.0]])]});}
            var Q28;
            {var subQ0=sQuery(id+"F2.wireOp",EDGE,"E60.27");var subQ1=sQuery(id+"F2.wireOp",EDGE,"E52");var subQ2=makeQuery(id+"F2.imprint","INTERSECT",VERTEX,{"disambiguationData":[OD(0.0)],"derivedFrom":[subQ1,subQ0]});Q28=makeQuery(id+"F2.imprint","IMPRINT",FACE,{"disambiguationData":[TD([[makeQuery(id+"F2.imprint","IMPRINT",EDGE,{"disambiguationData":[TD([[subQ2,-1.0]])],"derivedFrom":subQ1}),1.0]])]});}
            extrude(context, id + "F3", {"entities" : qUnion([Q0, Q1, Q2, Q3, Q4, Q5, Q6, Q7, Q8, Q9, Q10, Q11, Q12, Q13, Q14, Q15, Q16, Q17, Q18, Q19, Q20, Q21, Q22, Q23, Q24, Q25, Q26, Q27, Q28]), "depth" : 25.4 * mm});
        }
    });
